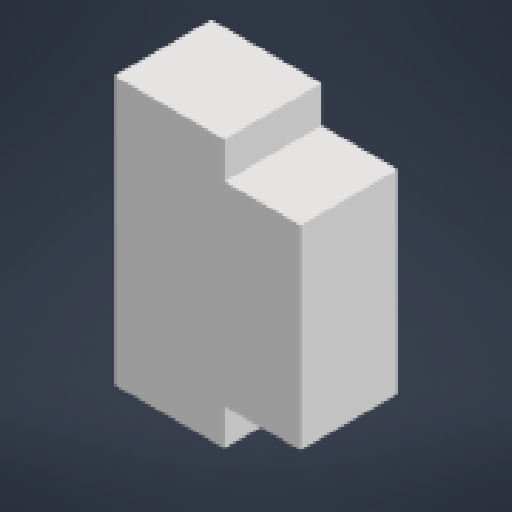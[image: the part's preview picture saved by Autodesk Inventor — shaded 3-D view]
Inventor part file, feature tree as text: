
AUTODESK INVENTOR PART (.ipt)
format: ipt  version: 2023 (Build 270158000, 158)  size: 114,176 bytes
history: native  units: in
note: dims shown in document units (in); Inventor stores cm internally (conversion verified against a paired STEP export)
features: extrude x1, sketch x1
ambient origin geometry x8: Origin, YZ Plane, XZ Plane, XY Plane, X Axis, Y Axis, Z Axis, Center Point
bodies: Solid1 (feature_tree)
feature tree (2):
  extrude  "Extrusion1"  Depth=0.065in
  sketch  "Sketch1"  dims[d0=0.0268in d1=0.065in d2=0.0185in d3=0.0236in d4=0.0236in d5=0.0236in d6=0.0in]
